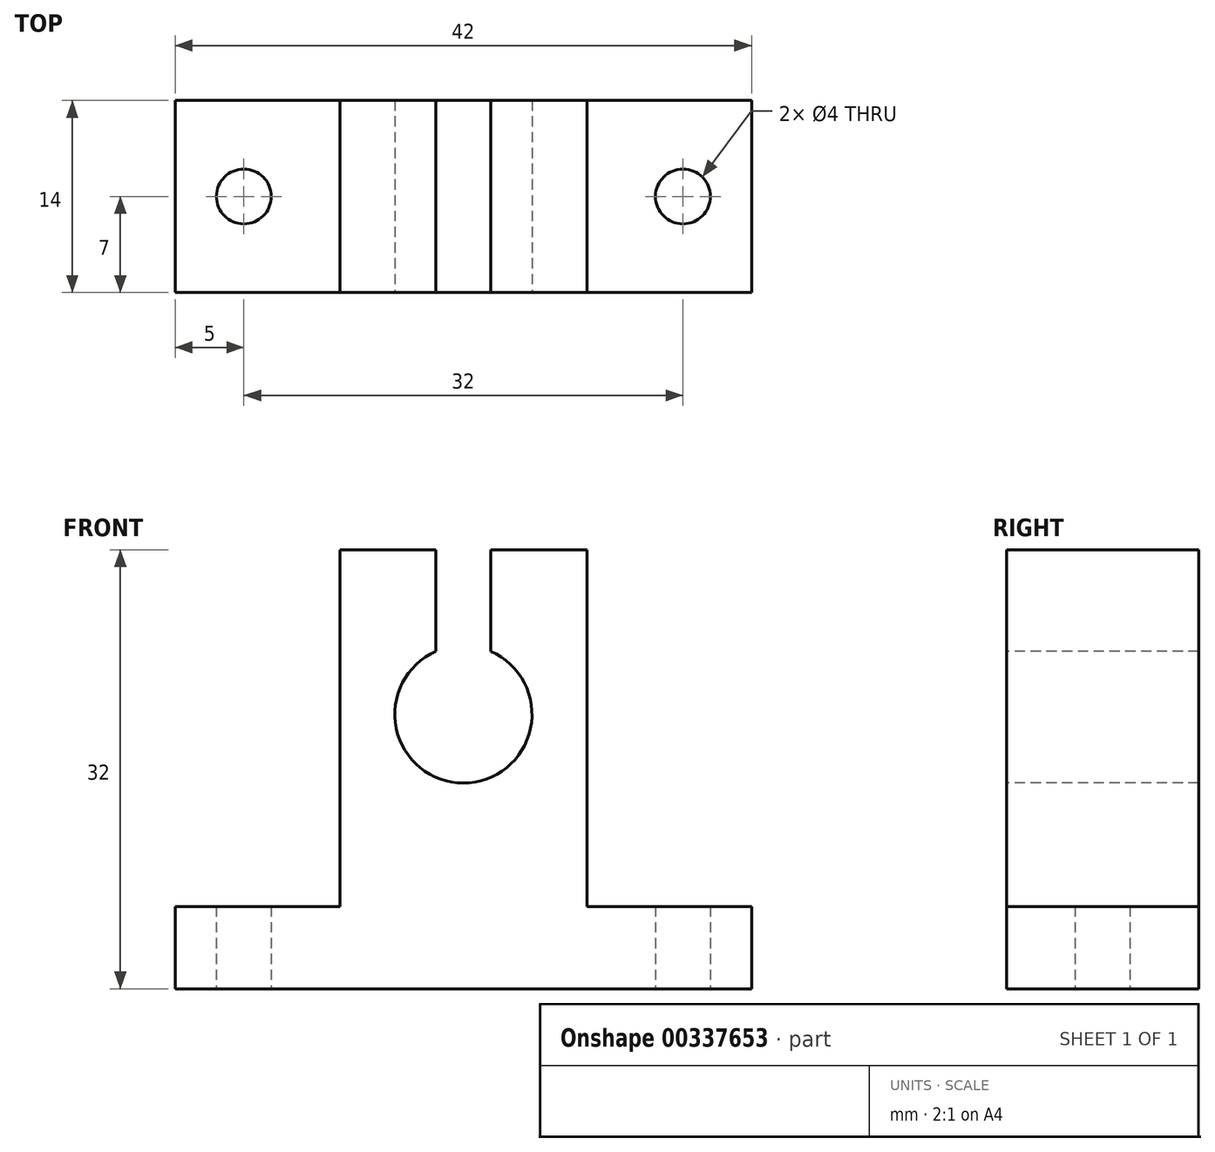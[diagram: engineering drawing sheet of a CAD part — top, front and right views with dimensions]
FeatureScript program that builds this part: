
annotation { "Feature Type Name" : "Feature", "Feature Type Description" : "" }
export const myFeature = defineFeature(function(context is Context, id is Id, definition is map)
    precondition{}
    {
        {
            var Q0;
            Q0=qCreatedBy(makeId("Top.planeOp"),FACE);
            var sketch = newSketch(context, id + "F0", { "sketchPlane" : qUnion([Q0])});
            skLineSegment(sketch, "E0.bottom", {"start": v(21, -7) * mm, "end": v(-21, -7) * mm});
            skLineSegment(sketch, "E0.top", {"start": v(21, 7) * mm, "end": v(-21, 7) * mm});
            skLineSegment(sketch, "E0.left", {"start": v(21, -7) * mm, "end": v(21, 7) * mm});
            skLineSegment(sketch, "E0.right", {"start": v(-21, -7) * mm, "end": v(-21, 7) * mm});
            skPoint(sketch, "E0.middle", {"position": v(0, 0) * mm});
            skSolve(sketch);
        }
        {
            var Q0;
            Q0=makeQuery(id+"F0.imprint","IMPRINT",FACE,{"disambiguationData":[TD([[makeQuery(id+"F0.imprint","IMPRINT",EDGE,{"derivedFrom":sQuery(id+"F0.wireOp",EDGE,"E0.bottom")}),-1.0]])]});
            extrude(context, id + "F1", {"entities" : qUnion([Q0]), "depth" : 6 * mm});
        }
        {
            var Q0;
            Q0=makeQuery(id+"F1.opExtrude","CAP_FACE",FACE,{"disambiguationData":[OSD([sQuery(id+"F0.wireOp",EDGE,"E0.bottom"),sQuery(id+"F0.wireOp",EDGE,"E0.top"),sQuery(id+"F0.wireOp",EDGE,"E0.left"),sQuery(id+"F0.wireOp",EDGE,"E0.right")])],"isStart":false});
            var sketch = newSketch(context, id + "F2", { "sketchPlane" : qUnion([Q0])});
            skLineSegment(sketch, "E1.bottom", {"start": v(9, -7) * mm, "end": v(-9, -7) * mm});
            skLineSegment(sketch, "E1.top", {"start": v(9, 7) * mm, "end": v(-9, 7) * mm});
            skLineSegment(sketch, "E1.left", {"start": v(9, -7) * mm, "end": v(9, 7) * mm});
            skLineSegment(sketch, "E1.right", {"start": v(-9, -7) * mm, "end": v(-9, 7) * mm});
            skPoint(sketch, "E1.middle", {"position": v(0, 0) * mm});
            skSolve(sketch);
        }
        {
            var Q0;
            Q0=makeQuery(id+"F2.imprint","IMPRINT",FACE,{"disambiguationData":[TD([[makeQuery(id+"F2.imprint","IMPRINT",EDGE,{"derivedFrom":sQuery(id+"F2.wireOp",EDGE,"E1.bottom")}),-1.0]])]});
            extrude(context, id + "F3", {"entities" : qUnion([Q0]), "operationType" : NewBodyOperationType.ADD, "depth" : 26 * mm});
        }
        {
            var Q0;
            Q0=makeQuery(id+"F3.boolean.opBoolean","MERGE",FACE,{"derivedFrom":[makeQuery(id+"F1.opExtrude","SWEPT_FACE",FACE,{"disambiguationData":[OSD([sQuery(id+"F0.wireOp",EDGE,"E0.bottom")])]}),makeQuery(id+"F3.opExtrude","SWEPT_FACE",FACE,{"disambiguationData":[OSD([sQuery(id+"F2.wireOp",EDGE,"E1.bottom")])]})]});
            var sketch = newSketch(context, id + "F4", { "sketchPlane" : qUnion([Q0])});
            skCircle(sketch, "E2", {"center": v(0, 20) * mm, "radius": 5 * mm});
            skSolve(sketch);
        }
        {
            var Q0;
            Q0=makeQuery(id+"F4.imprint","IMPRINT",FACE,{"disambiguationData":[TD([[makeQuery(id+"F4.imprint","IMPRINT",EDGE,{"derivedFrom":sQuery(id+"F4.wireOp",EDGE,"E2")}),1.0]])]});
            var Q1;
            Q1=sQuery(id+"F4.wireOp",EDGE,"E2");
            extrude(context, id + "F5", {"entities" : qUnion([Q0]), "operationType" : NewBodyOperationType.REMOVE, "surfaceEntities" : qUnion([Q1]), "endBound" : BoundingType.UP_TO_NEXT, "oppositeDirection" : true, "depth" : 25 * mm});
        }
        {
            var Q0;
            Q0=makeQuery(id+"F3.opExtrude","CAP_FACE",FACE,{"disambiguationData":[OSD([sQuery(id+"F2.wireOp",EDGE,"E1.bottom"),sQuery(id+"F2.wireOp",EDGE,"E1.top"),sQuery(id+"F2.wireOp",EDGE,"E1.left"),sQuery(id+"F2.wireOp",EDGE,"E1.right")])],"isStart":false});
            var sketch = newSketch(context, id + "F6", { "sketchPlane" : qUnion([Q0])});
            skSolve(sketch);
        }
        {
            var Q0;
            Q0=makeQuery(id+"F6.imprint","IMPRINT",FACE,{"disambiguationData":[TD([[makeQuery(id+"F6.imprint","IMPRINT",EDGE,{"derivedFrom":makeQuery(id+"F3.opExtrude","CAP_EDGE",EDGE,{"disambiguationData":[OSD([sQuery(id+"F2.wireOp",EDGE,"E1.bottom")])],"isStart":false})}),-1.0]])]});
            var sketch = newSketch(context, id + "F7", { "sketchPlane" : qUnion([Q0])});
            skLineSegment(sketch, "E3.bottom", {"start": v(2, -7) * mm, "end": v(-2, -7) * mm});
            skLineSegment(sketch, "E3.top", {"start": v(2, 7) * mm, "end": v(-2, 7) * mm});
            skLineSegment(sketch, "E3.left", {"start": v(2, -7) * mm, "end": v(2, 7) * mm});
            skLineSegment(sketch, "E3.right", {"start": v(-2, -7) * mm, "end": v(-2, 7) * mm});
            skPoint(sketch, "E3.middle", {"position": v(0, 0) * mm});
            skSolve(sketch);
        }
        {
            var Q0;
            Q0 = qSketchRegion(id + "F7", true);
            extrude(context, id + "F8", {"entities" : qUnion([Q0]), "operationType" : NewBodyOperationType.REMOVE, "oppositeDirection" : true, "depth" : 14 * mm});
        }
        {
            var Q0;
            Q0=makeQuery(id+"F1.opExtrude","CAP_FACE",FACE,{"disambiguationData":[OSD([sQuery(id+"F0.wireOp",EDGE,"E0.bottom"),sQuery(id+"F0.wireOp",EDGE,"E0.top"),sQuery(id+"F0.wireOp",EDGE,"E0.left"),sQuery(id+"F0.wireOp",EDGE,"E0.right")])],"isStart":true});
            var sketch = newSketch(context, id + "F9", { "sketchPlane" : qUnion([Q0])});
            skLineSegment(sketch, "E4", {"start": v(21, 0) * mm, "end": v(-21, 0) * mm, "construction": true});
            skSolve(sketch);
        }
        {
            var Q0;
            Q0=makeQuery(id+"F9.imprint","IMPRINT",FACE,{"disambiguationData":[TD([[makeQuery(id+"F9.imprint","IMPRINT",EDGE,{"derivedFrom":makeQuery(id+"F1.opExtrude","CAP_EDGE",EDGE,{"disambiguationData":[OSD([sQuery(id+"F0.wireOp",EDGE,"E0.bottom")])],"isStart":true})}),1.0]])]});
            var sketch = newSketch(context, id + "F10", { "sketchPlane" : qUnion([Q0])});
            skPoint(sketch, "E5", {"position": v(0, 0) * mm});
            skLineSegment(sketch, "E6", {"start": v(0, 0) * mm, "end": v(16, 0) * mm, "construction": true});
            skLineSegment(sketch, "E7", {"start": v(0, 0) * mm, "end": v(-16, 0) * mm, "construction": true});
            skCircle(sketch, "E8", {"center": v(16, 0) * mm, "radius": 2 * mm});
            skCircle(sketch, "E9", {"center": v(-16, 0) * mm, "radius": 2 * mm});
            skSolve(sketch);
        }
        {
            var Q0;
            Q0=makeQuery(id+"F10.imprint","IMPRINT",FACE,{"disambiguationData":[TD([[makeQuery(id+"F10.imprint","IMPRINT",EDGE,{"derivedFrom":sQuery(id+"F10.wireOp",EDGE,"E8")}),1.0]])]});
            var Q1;
            Q1=makeQuery(id+"F10.imprint","IMPRINT",FACE,{"disambiguationData":[TD([[makeQuery(id+"F10.imprint","IMPRINT",EDGE,{"derivedFrom":sQuery(id+"F10.wireOp",EDGE,"E9")}),1.0]])]});
            var Q2;
            Q2=sQuery(id+"F10.wireOp",EDGE,"E8");
            var Q3;
            Q3=sQuery(id+"F10.wireOp",EDGE,"E9");
            extrude(context, id + "F11", {"entities" : qUnion([Q0, Q1]), "operationType" : NewBodyOperationType.REMOVE, "surfaceEntities" : qUnion([Q2, Q3]), "oppositeDirection" : true, "depth" : 25 * mm});
        }
    });
